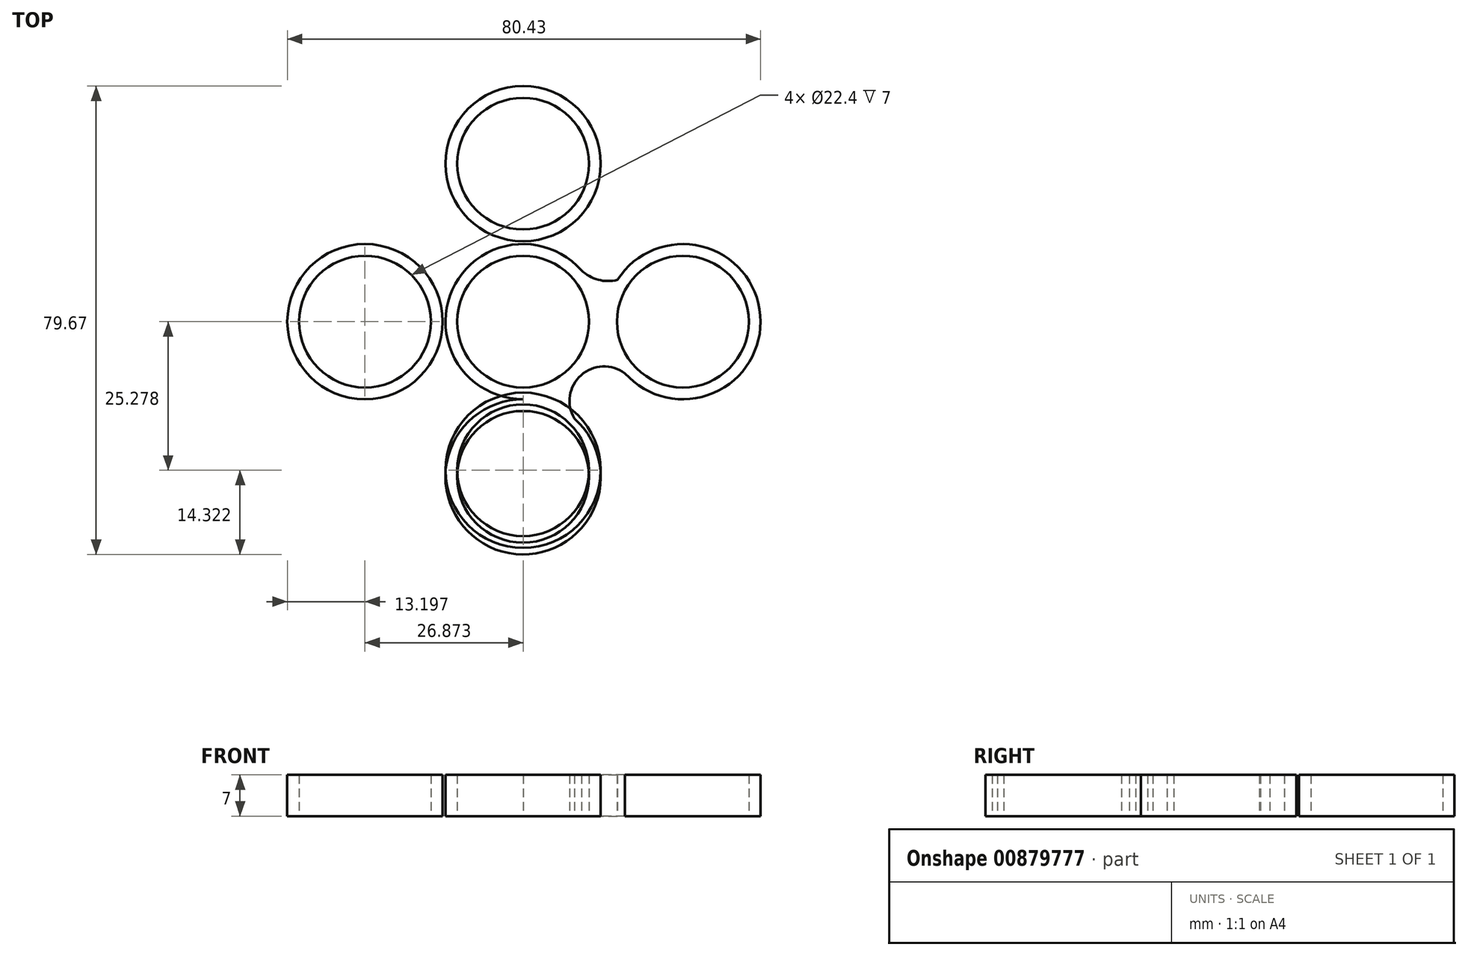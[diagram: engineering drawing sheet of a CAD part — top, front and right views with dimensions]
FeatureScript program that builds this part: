
annotation { "Feature Type Name" : "Feature", "Feature Type Description" : "" }
export const myFeature = defineFeature(function(context is Context, id is Id, definition is map)
    precondition{}
    {
        {
            var Q0;
            Q0=qCreatedBy(makeId("Top.planeOp"),FACE);
            var sketch = newSketch(context, id + "F0", { "sketchPlane" : qUnion([Q0])});
            skCircle(sketch, "E0", {"center": v(0, 0) * mm, "radius": 11.2 * mm});
            skCircle(sketch, "E1", {"center": v(0, 0) * mm, "radius": 13.2 * mm});
            skCircle(sketch, "E2", {"center": v(0, 26.87) * mm, "radius": 11.2 * mm});
            skCircle(sketch, "E3", {"center": v(0, 26.87) * mm, "radius": 13.2 * mm});
            skCircle(sketch, "E4", {"center": v(-26.87, 0) * mm, "radius": 11.2 * mm});
            skCircle(sketch, "E5", {"center": v(-26.87, 0) * mm, "radius": 13.2 * mm});
            skCircle(sketch, "E6", {"center": v(27.16, 0) * mm, "radius": 11.2 * mm});
            skCircle(sketch, "E7", {"center": v(27.16, 0) * mm, "radius": 13.2 * mm});
            skCircle(sketch, "E8", {"center": v(0, -26.4) * mm, "radius": 11.2 * mm});
            skCircle(sketch, "E9", {"center": v(0, -26.4) * mm, "radius": 13.2 * mm});
            skArc(sketch, "E10", {"start": v(9.54, 17.75) * mm, "mid": v(11.22, 7.75) * mm, "end": v(20.65, 11.48) * mm});
            skArc(sketch, "E11", {"start": v(-17.65, 9.44) * mm, "mid": v(-9.58, 9.38) * mm, "end": v(-9.23, 17.44) * mm});
            skArc(sketch, "E12", {"start": v(-8.71, -16.48) * mm, "mid": v(-9.67, -9.36) * mm, "end": v(-16.81, -8.55) * mm});
            skArc(sketch, "E13", {"start": v(17.3, -8.78) * mm, "mid": v(9.86, -9.1) * mm, "end": v(8.7, -16.47) * mm});
            skSolve(sketch);
        }
        {
            var Q0;
            Q0=qCreatedBy(makeId("Top.planeOp"),FACE);
            var sketch = newSketch(context, id + "F1", { "sketchPlane" : qUnion([Q0])});
            skCircle(sketch, "E14", {"center": v(0, -25.28) * mm, "radius": 11.2 * mm});
            skCircle(sketch, "E15", {"center": v(0, -25.28) * mm, "radius": 13.2 * mm});
            skArc(sketch, "E16", {"start": v(-10.55, -17.34) * mm, "mid": v(-9.34, -8.8) * mm, "end": v(-17.96, -8.48) * mm});
            skArc(sketch, "E17", {"start": v(18.25, -9.63) * mm, "mid": v(9.3, -9.33) * mm, "end": v(11.08, -18.1) * mm});
            skArc(sketch, "E18", {"start": v(9.63, 16.81) * mm, "mid": v(10.83, 8.1) * mm, "end": v(19.11, 11.07) * mm});
            skArc(sketch, "E19", {"start": v(-17.68, 9.63) * mm, "mid": v(-8.7, 9.81) * mm, "end": v(-10.78, 18.54) * mm});
            skSolve(sketch);
        }
        {
            var Q0;
            Q0 = qSketchRegion(id + "F1", true);
            var Q1;
            Q1 = qSketchRegion(id + "F0", true);
            extrude(context, id + "F2", {"entities" : qUnion([Q0, Q1]), "depth" : 7 * mm, "offsetDistance" : 25 * mm});
        }
        {
            var Q0;
            Q0 = qSketchRegion(id + "F0", true);
            extrude(context, id + "F3", {"entities" : qUnion([Q0]), "depth" : 7 * mm, "offsetDistance" : 25 * mm});
        }
        {
            var Q0;
            Q0 = qSketchRegion(id + "F0", true);
            extrude(context, id + "F4", {"entities" : qUnion([Q0]), "depth" : 7 * mm, "offsetDistance" : 25 * mm});
        }
    });
